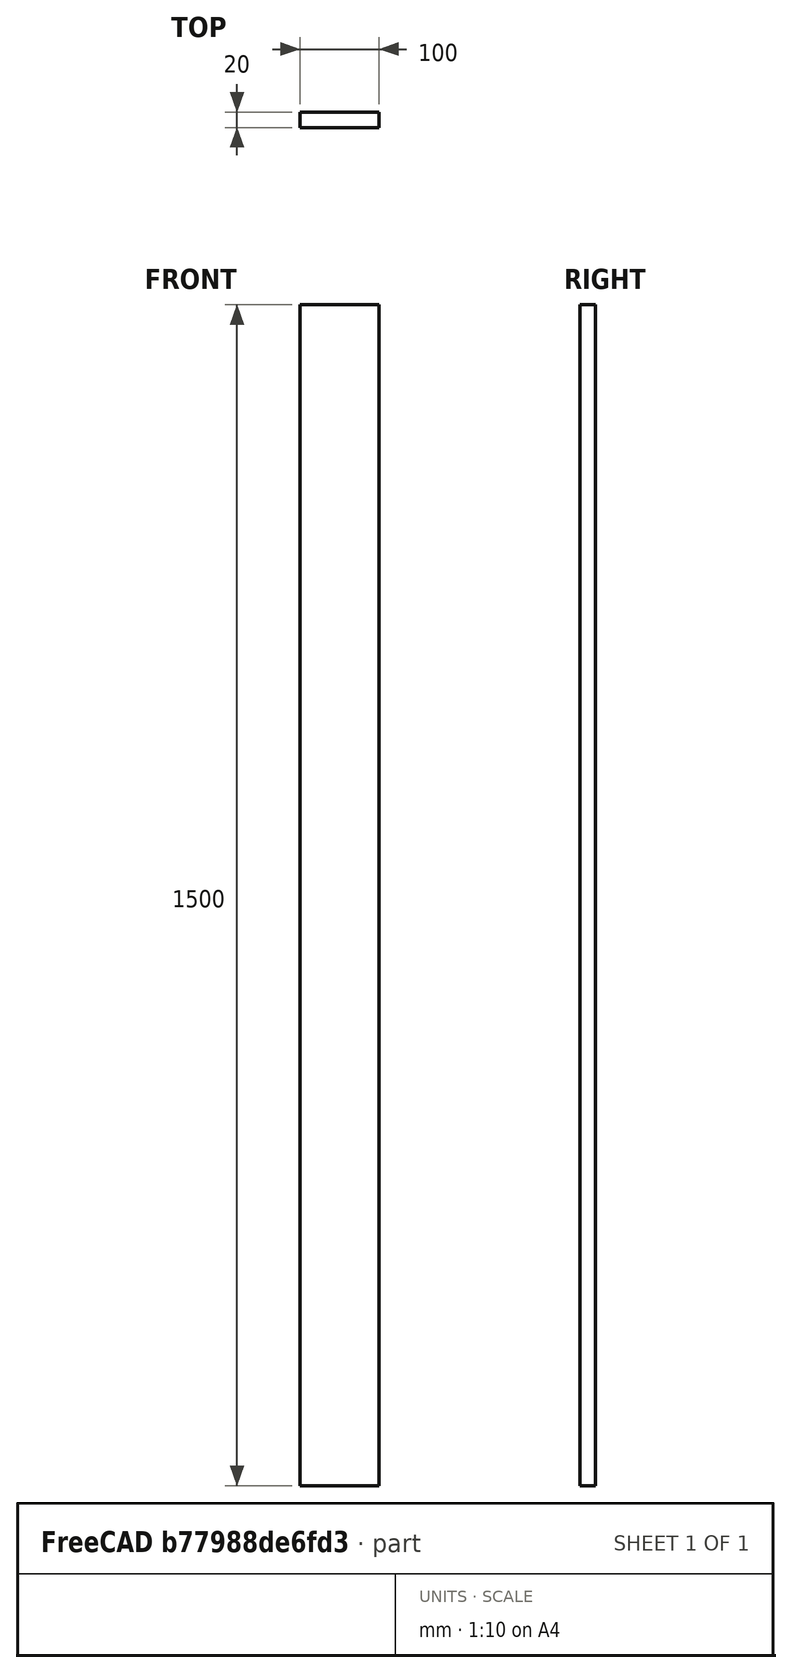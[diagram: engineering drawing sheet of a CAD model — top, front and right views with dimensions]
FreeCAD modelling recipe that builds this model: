
FCSTD DOCUMENT  (FreeCAD 0.18R4 (GitTag))
Label: aframe-1
License: All rights reserved
LicenseURL: http://en.wikipedia.org/wiki/All_rights_reserved
objects: App::Part×1, Sketcher::SketchObject×1, PartDesign::Pad×1, PartDesign::Body×1
note: 4 computed .brp shape members not serialized (recipe doc carries the construction recipe); baked Part::Feature solids carry a one-line shape summary decoded from their .brp

FEATURE [App::Part] Part
  Origin = -> Origin
FEATURE [Sketcher::SketchObject] Sketch
  MapMode = 5
  Support = -> [XY_Plane001]
  sketch-geometry (4):
    g0: LineSegment StartX=0 StartY=0 StartZ=0 EndX=-100 EndY=0 EndZ=0
    g1: LineSegment StartX=-100 StartY=0 StartZ=0 EndX=-100 EndY=20 EndZ=0
    g2: LineSegment StartX=-100 StartY=20 StartZ=0 EndX=0 EndY=20 EndZ=0
    g3: LineSegment StartX=0 StartY=20 StartZ=0 EndX=0 EndY=0 EndZ=0
  constraints (11):
    c: Coincident(g0,g1)
    c: Coincident(g1,g2)
    c: Coincident(g2,g3)
    c: Coincident(g3,g0)
    c: Horizontal(g0)
    c: Horizontal(g2)
    c: Vertical(g1)
    c: Vertical(g3)
    c: DistanceY(g1,g1) = 20
    c: DistanceX(g0,g0) = 100
    c: Coincident(g0,g-1)
FEATURE [PartDesign::Pad] Pad
  Length = 1500
  Length2 = 100
  Profile = -> Sketch
  Type = 0
FEATURE [PartDesign::Body] Body
  Group = -> [Sketch,Pad]
  Origin = -> Origin001
  Tip = -> Pad
